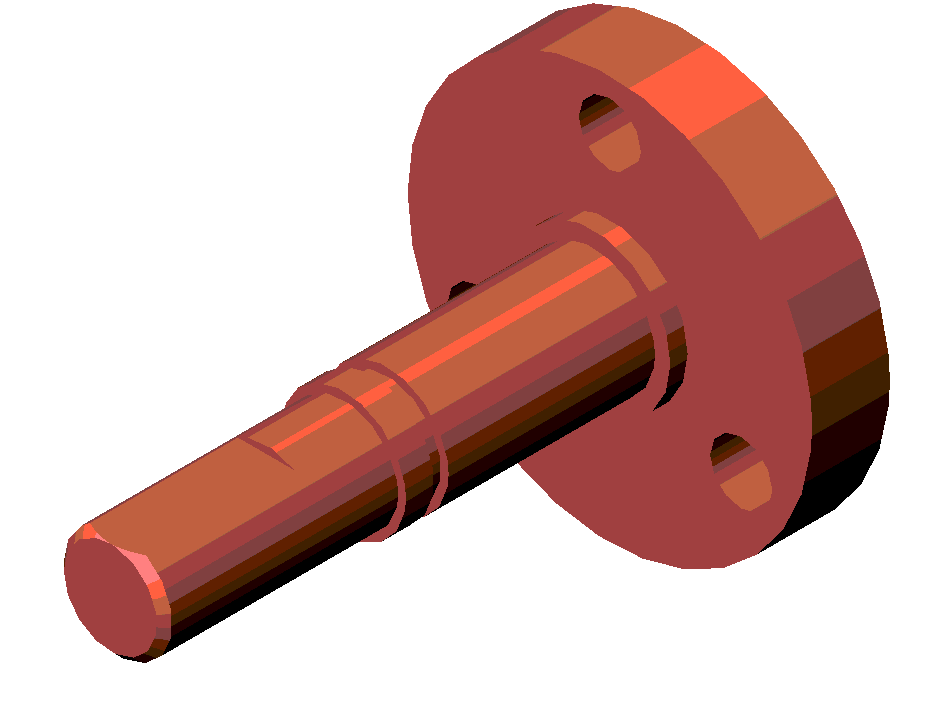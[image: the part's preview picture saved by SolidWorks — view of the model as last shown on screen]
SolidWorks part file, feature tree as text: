
SOLIDWORKS PART (.sldprt)
format: sldprt  version: not decoded by parser v0  size: 150,528 bytes
history: native  units: mm
features: sketch x8, extrude x4, plane x3, pattern_circular x3, material x1, cut_extrude x1, cut_revolve x1, chamfer x1 (+10 scaffold rows collapsed)
feature tree (32):
  scaffold x10  (default folders/planes/origin — collapsed)
  material  "Matériau <non spécifié>"
  plane  "Plan1"
  plane  "Plan2"
  plane  "Plan3"
  sketch  "Esquisse1"  dims[D1=26.0mm]
  extrude  "Base-Extrusion"  Depth=5mm
  sketch  "Esquisse2"  dims[D1=10.0mm]
  extrude  "Boss.-Extru.1"  Depth=1.1mm
  sketch  "Esquisse3"  dims[D1=8.0mm]
  extrude  "Boss.-Extru.2"  Depth=16mm
  sketch  "Esquisse4"  dims[D1=7.0mm]
  extrude  "Boss.-Extru.3"  Depth=15mm
  sketch  "Esquisse5"  dims[D2=4.0mm D1=9.75mm]
  cut_extrude  "Enlèv. mat.-Extru.1"  [1 undecoded]
  pattern_circular  "Répétition circulaire1"  Count=3 Angle=120deg
  sketch  "Esquisse6"  dims[D1=14.2mm D2=0.94mm D3=7.0mm D4=~3.116395mm]
  cut_revolve  "Enlèvement de matière-Révolution1"  Angle=360deg
  chamfer  "Chanfrein1"  Distance=0.5mm Angle=45deg
  sketch  "Esquisse8"  dims[D1=3.0mm]
  pattern_circular  "Enlèv. mat.-Extru.2"  [2 undecoded]
  sketch  "Esquisse9"  dims[D1=12.0mm]
  pattern_circular  "Enlèv. mat.-Extru.3"  [2 undecoded]
decode coverage: 15 of 18 modeling features carry decoded parameters
note: ~ marks probable driven/reference dimensions
note: 5 parameter values undecoded
note: suppression state not decoded; provenance and decode notes live in map.json
